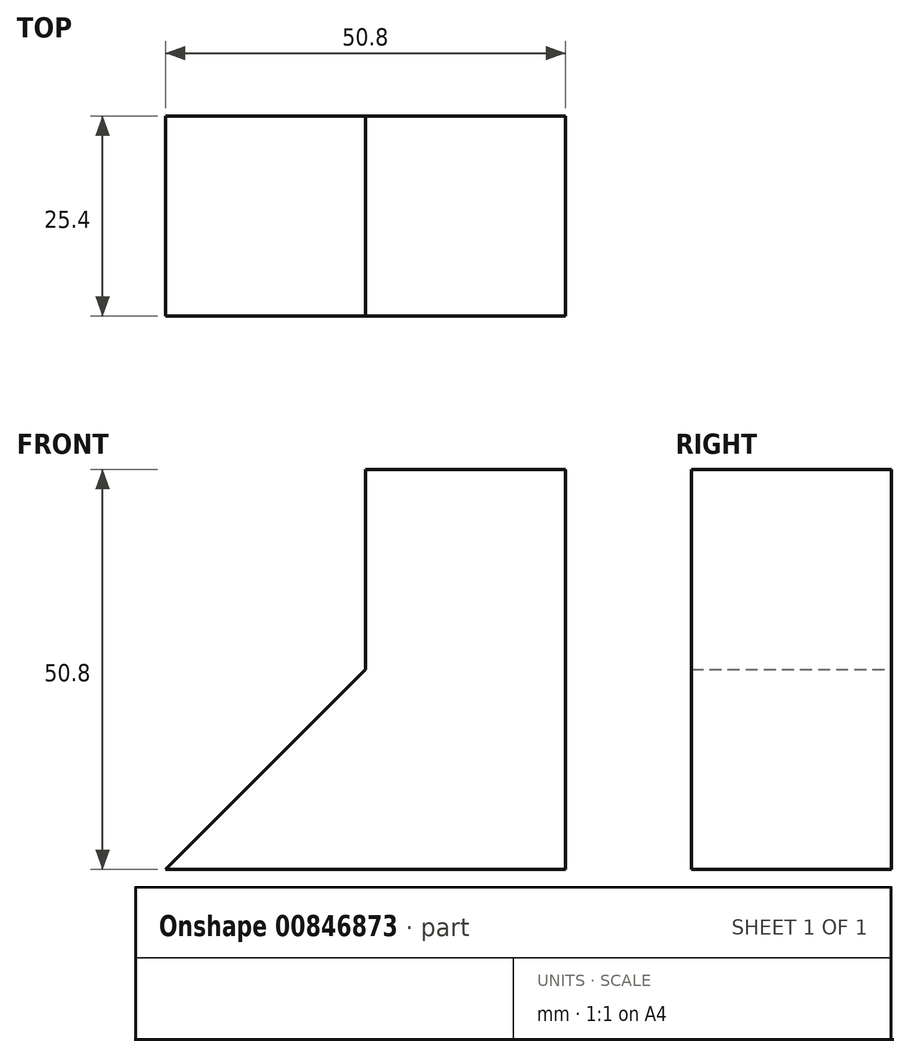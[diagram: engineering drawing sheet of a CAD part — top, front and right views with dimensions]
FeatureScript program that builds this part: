
annotation { "Feature Type Name" : "Feature", "Feature Type Description" : "" }
export const myFeature = defineFeature(function(context is Context, id is Id, definition is map)
    precondition{}
    {
        {
            var Q0;
            Q0=qCreatedBy(makeId("Front.planeOp"),FACE);
            var sketch = newSketch(context, id + "F0", { "sketchPlane" : qUnion([Q0])});
            skLineSegment(sketch, "E0", {"start": v(0, 0) * mm, "end": v(0, 50.8) * mm});
            skLineSegment(sketch, "E1", {"start": v(0, 0) * mm, "end": v(-50.8, 0) * mm});
            skLineSegment(sketch, "E2", {"start": v(0, 50.8) * mm, "end": v(-25.4, 50.8) * mm});
            skLineSegment(sketch, "E3", {"start": v(-25.4, 50.8) * mm, "end": v(-25.4, 25.4) * mm});
            skLineSegment(sketch, "E4", {"start": v(-25.4, 25.4) * mm, "end": v(-50.8, 0) * mm});
            skSolve(sketch);
        }
        {
            var Q0;
            Q0=qSketchRegion(id+"F0",true);
            extrude(context, id + "F1", {"entities" : qUnion([Q0]), "depth" : 25.4 * mm, "offsetDistance" : 25.4 * mm});
        }
    });
